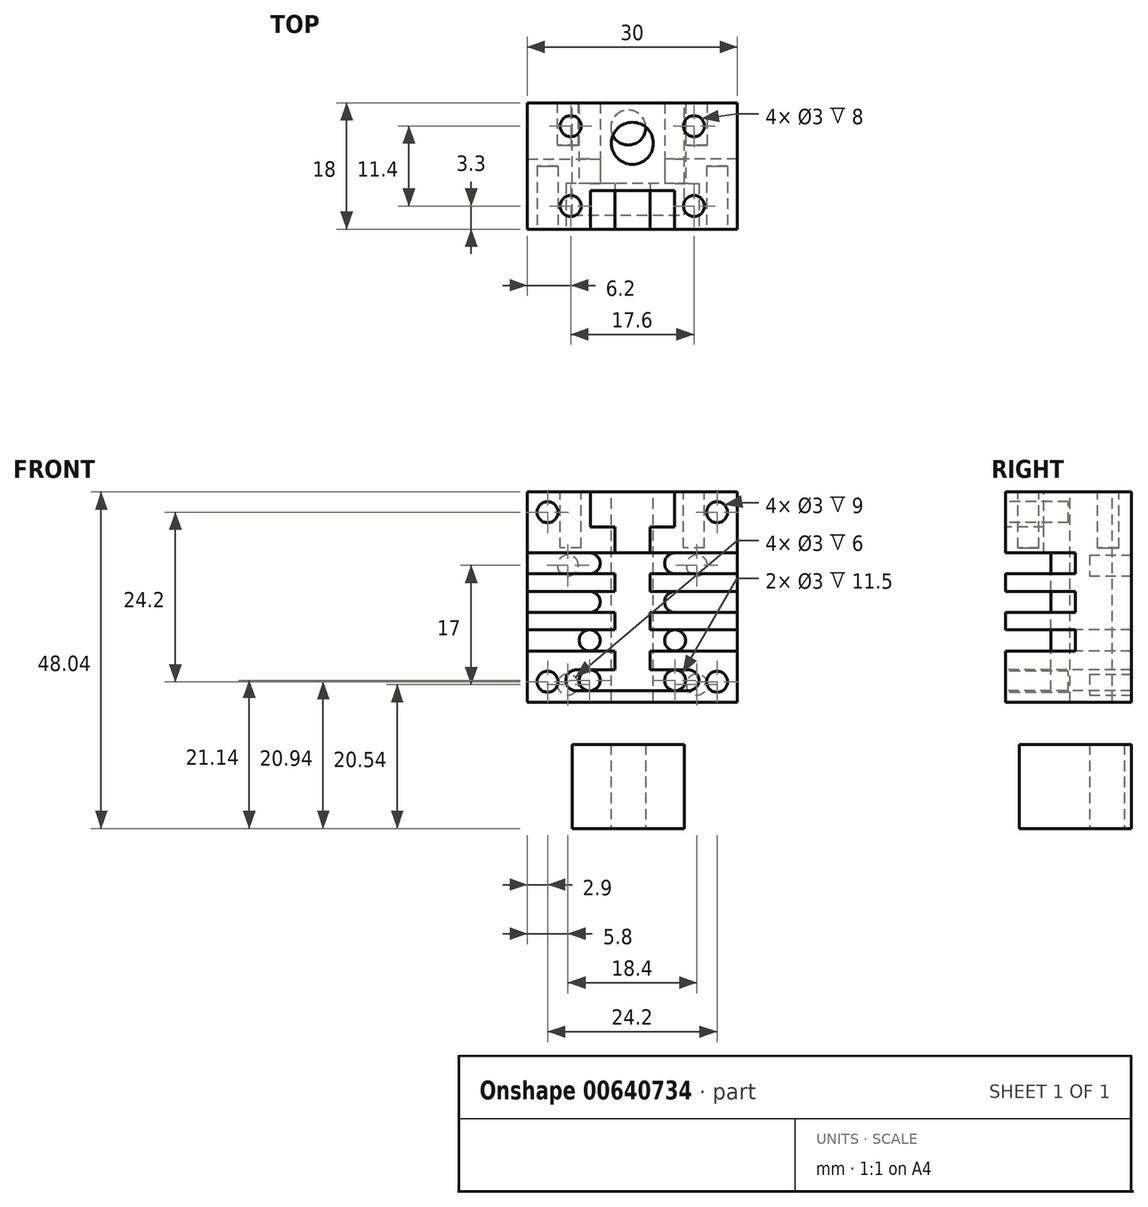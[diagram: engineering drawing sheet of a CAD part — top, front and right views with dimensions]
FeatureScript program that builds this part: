
annotation { "Feature Type Name" : "Feature", "Feature Type Description" : "" }
export const myFeature = defineFeature(function(context is Context, id is Id, definition is map)
    precondition{}
    {
        {
            var Q0;
            Q0=qCreatedBy(makeId("Front.planeOp"),FACE);
            var sketch = newSketch(context, id + "F0", { "sketchPlane" : qUnion([Q0])});
            skLineSegment(sketch, "E0.bottom", {"start": v(15, -15) * mm, "end": v(-15, -15) * mm});
            skLineSegment(sketch, "E0.top", {"start": v(15, 15) * mm, "end": v(-15, 15) * mm});
            skLineSegment(sketch, "E0.left", {"start": v(15, -15) * mm, "end": v(15, 15) * mm});
            skLineSegment(sketch, "E0.right", {"start": v(-15, -15) * mm, "end": v(-15, 15) * mm});
            skPoint(sketch, "E0.middle", {"position": v(0, 0) * mm});
            skSolve(sketch);
        }
        {
            var Q0;
            Q0 = qSketchRegion(id + "F0", true);
            extrude(context, id + "F1", {"entities" : qUnion([Q0]), "depth" : 18 * mm, "offsetDistance" : 25 * mm});
        }
        {
            var Q0;
            Q0=makeQuery(id+"F1.opExtrude","CAP_FACE",FACE,{"disambiguationData":[OSD([sQuery(id+"F0.wireOp",EDGE,"E0.bottom"),sQuery(id+"F0.wireOp",EDGE,"E0.top"),sQuery(id+"F0.wireOp",EDGE,"E0.left"),sQuery(id+"F0.wireOp",EDGE,"E0.right")])],"isStart":false});
            var sketch = newSketch(context, id + "F2", { "sketchPlane" : qUnion([Q0])});
            skLineSegment(sketch, "E1.bottom", {"start": v(6, 10) * mm, "end": v(-6, 10) * mm});
            skLineSegment(sketch, "E1.top", {"start": v(6, 20) * mm, "end": v(-6, 20) * mm});
            skLineSegment(sketch, "E1.left", {"start": v(6, 10) * mm, "end": v(6, 20) * mm});
            skLineSegment(sketch, "E1.right", {"start": v(-6, 10) * mm, "end": v(-6, 20) * mm});
            skPoint(sketch, "E1.middle", {"position": v(0, 15) * mm});
            skLineSegment(sketch, "E2.bottom", {"start": v(2.5, -13.4) * mm, "end": v(-2.5, -13.4) * mm});
            skLineSegment(sketch, "E2.top", {"start": v(2.5, 13.4) * mm, "end": v(-2.5, 13.4) * mm});
            skLineSegment(sketch, "E2.left", {"start": v(2.5, -13.4) * mm, "end": v(2.5, 13.4) * mm});
            skLineSegment(sketch, "E2.right", {"start": v(-2.5, -13.4) * mm, "end": v(-2.5, 13.4) * mm});
            skPoint(sketch, "E2.middle", {"position": v(0, 0) * mm});
            skSolve(sketch);
        }
        {
            var Q0;
            Q0 = qSketchRegion(id + "F2", true);
            extrude(context, id + "F3", {"entities" : qUnion([Q0]), "operationType" : NewBodyOperationType.REMOVE, "oppositeDirection" : true, "depth" : 5.5 * mm, "offsetDistance" : 25 * mm});
        }
        {
            var Q0;
            Q0=makeQuery(id+"F1.opExtrude","CAP_FACE",FACE,{"disambiguationData":[OSD([sQuery(id+"F0.wireOp",EDGE,"E0.bottom"),sQuery(id+"F0.wireOp",EDGE,"E0.top"),sQuery(id+"F0.wireOp",EDGE,"E0.left"),sQuery(id+"F0.wireOp",EDGE,"E0.right")])],"isStart":false});
            var sketch = newSketch(context, id + "F4", { "sketchPlane" : qUnion([Q0])});
            skLineSegment(sketch, "E3", {"start": v(13.15, -15) * mm, "end": v(13.15, -7.7) * mm, "construction": true});
            skLineSegment(sketch, "E4", {"start": v(13.15, -7.7) * mm, "end": v(13.15, -4.7) * mm, "construction": true});
            skLineSegment(sketch, "E5", {"start": v(13.15, -4.7) * mm, "end": v(13.15, -2.2) * mm, "construction": true});
            skLineSegment(sketch, "E6", {"start": v(13.15, -2.2) * mm, "end": v(13.15, 0.8) * mm, "construction": true});
            skLineSegment(sketch, "E7", {"start": v(13.15, 0.8) * mm, "end": v(13.15, 3.3) * mm, "construction": true});
            skLineSegment(sketch, "E8", {"start": v(13.15, 3.3) * mm, "end": v(13.15, 6.3) * mm, "construction": true});
            skLineSegment(sketch, "E9", {"start": v(13.15, 6.3) * mm, "end": v(13.15, 14.8) * mm, "construction": true});
            skLineSegment(sketch, "E10.bottom", {"start": v(15, -7.7) * mm, "end": v(-15, -7.7) * mm});
            skLineSegment(sketch, "E10.top", {"start": v(15, -4.7) * mm, "end": v(-15, -4.7) * mm});
            skLineSegment(sketch, "E10.left", {"start": v(15, -7.7) * mm, "end": v(15, -4.7) * mm});
            skLineSegment(sketch, "E10.right", {"start": v(-15, -7.7) * mm, "end": v(-15, -4.7) * mm});
            skLineSegment(sketch, "E11.bottom", {"start": v(15, -2.2) * mm, "end": v(-15, -2.2) * mm});
            skLineSegment(sketch, "E11.top", {"start": v(15, 0.8) * mm, "end": v(-15, 0.8) * mm});
            skLineSegment(sketch, "E11.left", {"start": v(15, -2.2) * mm, "end": v(15, 0.8) * mm});
            skLineSegment(sketch, "E11.right", {"start": v(-15, -2.2) * mm, "end": v(-15, 0.8) * mm});
            skLineSegment(sketch, "E12.bottom", {"start": v(15, 3.3) * mm, "end": v(-15, 3.3) * mm});
            skLineSegment(sketch, "E12.top", {"start": v(15, 6.3) * mm, "end": v(-15, 6.3) * mm});
            skLineSegment(sketch, "E12.left", {"start": v(15, 3.3) * mm, "end": v(15, 6.3) * mm});
            skLineSegment(sketch, "E12.right", {"start": v(-15, 3.3) * mm, "end": v(-15, 6.3) * mm});
            skPoint(sketch, "E13.startSnap0", {"position": v(13.15, -11.35) * mm});
            skLineSegment(sketch, "E14", {"start": v(0, -7.7) * mm, "end": v(0, -10.4) * mm, "construction": true});
            skLineSegment(sketch, "E15", {"start": v(0, -10.4) * mm, "end": v(0, -11.9) * mm, "construction": true});
            skLineSegment(sketch, "E16", {"start": v(8, -11.9) * mm, "end": v(15, -11.9) * mm, "construction": true});
            skLineSegment(sketch, "E17", {"start": v(8, -11.9) * mm, "end": v(-8, -11.9) * mm, "construction": true});
            skArc(sketch, "E18.0.startCap", {"start": v(8, -10.4) * mm, "mid": v(9.5, -11.9) * mm, "end": v(8, -13.4) * mm});
            skArc(sketch, "E18.0.endCap", {"start": v(-8, -13.4) * mm, "mid": v(-9.5, -11.9) * mm, "end": v(-8, -10.4) * mm});
            skLineSegment(sketch, "E18.0.left", {"start": v(8, -13.4) * mm, "end": v(-8, -13.4) * mm});
            skLineSegment(sketch, "E18.0.right", {"start": v(8, -10.4) * mm, "end": v(-8, -10.4) * mm});
            skLineSegment(sketch, "E19", {"start": v(2.5, 3.3) * mm, "end": v(2.5, 0.8) * mm});
            skLineSegment(sketch, "E20", {"start": v(2.5, -2.2) * mm, "end": v(2.5, -4.7) * mm});
            skLineSegment(sketch, "E21", {"start": v(-2.5, 3.3) * mm, "end": v(-2.5, 0.8) * mm});
            skLineSegment(sketch, "E22", {"start": v(-2.5, -2.2) * mm, "end": v(-2.5, -4.7) * mm});
            skLineSegment(sketch, "E23", {"start": v(2.5, -7.7) * mm, "end": v(2.5, -10.4) * mm});
            skLineSegment(sketch, "E24", {"start": v(-2.5, -7.7) * mm, "end": v(-2.5, -10.4) * mm});
            skSolve(sketch);
        }
        {
            var Q0;
            Q0 = qSketchRegion(id + "F4", true);
            extrude(context, id + "F5", {"entities" : qUnion([Q0]), "operationType" : NewBodyOperationType.REMOVE, "oppositeDirection" : true, "depth" : 6.5 * mm, "offsetDistance" : 25 * mm});
        }
        {
            var Q0;
            Q0=makeQuery(id+"F5.boolean.opBoolean","COPY",FACE,{"derivedFrom":makeQuery(id+"F5.opExtrude","CAP_FACE",FACE,{"disambiguationData":[OSD([sQuery(id+"F4.wireOp",EDGE,"E10.bottom"),sQuery(id+"F4.wireOp",EDGE,"E10.top"),sQuery(id+"F4.wireOp",EDGE,"E10.left"),sQuery(id+"F4.wireOp",EDGE,"E10.right"),sQuery(id+"F4.wireOp",EDGE,"E11.bottom"),sQuery(id+"F4.wireOp",EDGE,"E11.top"),sQuery(id+"F4.wireOp",EDGE,"E11.left"),sQuery(id+"F4.wireOp",EDGE,"E11.right"),sQuery(id+"F4.wireOp",EDGE,"E12.bottom"),sQuery(id+"F4.wireOp",EDGE,"E12.top"),sQuery(id+"F4.wireOp",EDGE,"E12.left"),sQuery(id+"F4.wireOp",EDGE,"E12.right"),sQuery(id+"F4.wireOp",EDGE,"E18.0.startCap"),sQuery(id+"F4.wireOp",EDGE,"E18.0.endCap"),sQuery(id+"F4.wireOp",EDGE,"E18.0.left"),sQuery(id+"F4.wireOp",EDGE,"E18.0.right"),sQuery(id+"F4.wireOp",EDGE,"E19"),sQuery(id+"F4.wireOp",EDGE,"E20"),sQuery(id+"F4.wireOp",EDGE,"E21"),sQuery(id+"F4.wireOp",EDGE,"E22"),sQuery(id+"F4.wireOp",EDGE,"E23"),sQuery(id+"F4.wireOp",EDGE,"E24")])],"isStart":false})});
            var sketch = newSketch(context, id + "F6", { "sketchPlane" : qUnion([Q0])});
            skLineSegment(sketch, "E25", {"start": v(-17, 4.8) * mm, "end": v(-6.1, 4.8) * mm, "construction": true});
            skPoint(sketch, "E25.startSnap0", {"position": v(-15, 4.8) * mm});
            skLineSegment(sketch, "E26", {"start": v(-17, -0.7) * mm, "end": v(-6.1, -0.7) * mm, "construction": true});
            skPoint(sketch, "E26.startSnap0", {"position": v(-15, -0.7) * mm});
            skLineSegment(sketch, "E27", {"start": v(-17, -6.2) * mm, "end": v(-6.1, -6.2) * mm, "construction": true});
            skPoint(sketch, "E27.startSnap0", {"position": v(-15, -6.2) * mm});
            skLineSegment(sketch, "E28", {"start": v(17, 4.8) * mm, "end": v(6.1, 4.8) * mm, "construction": true});
            skPoint(sketch, "E28.startSnap0", {"position": v(15, 4.8) * mm});
            skLineSegment(sketch, "E29", {"start": v(17, -0.7) * mm, "end": v(6.1, -0.7) * mm, "construction": true});
            skPoint(sketch, "E29.startSnap0", {"position": v(15, -0.7) * mm});
            skLineSegment(sketch, "E30", {"start": v(17, -6.2) * mm, "end": v(6.1, -6.2) * mm, "construction": true});
            skPoint(sketch, "E30.startSnap0", {"position": v(15, -6.2) * mm});
            skArc(sketch, "E31.0.startCap", {"start": v(-17, 3.3) * mm, "mid": v(-18.5, 4.8) * mm, "end": v(-17, 6.3) * mm});
            skArc(sketch, "E31.0.endCap", {"start": v(-6.1, 6.3) * mm, "mid": v(-4.6, 4.8) * mm, "end": v(-6.1, 3.3) * mm});
            skLineSegment(sketch, "E31.0.left", {"start": v(-17, 6.3) * mm, "end": v(-6.1, 6.3) * mm});
            skLineSegment(sketch, "E31.0.right", {"start": v(-17, 3.3) * mm, "end": v(-6.1, 3.3) * mm});
            skArc(sketch, "E31.1.startCap", {"start": v(-17, -2.2) * mm, "mid": v(-18.5, -0.7) * mm, "end": v(-17, 0.8) * mm});
            skArc(sketch, "E31.1.endCap", {"start": v(-6.1, 0.8) * mm, "mid": v(-4.6, -0.7) * mm, "end": v(-6.1, -2.2) * mm});
            skLineSegment(sketch, "E31.1.left", {"start": v(-17, 0.8) * mm, "end": v(-6.1, 0.8) * mm});
            skLineSegment(sketch, "E31.1.right", {"start": v(-17, -2.2) * mm, "end": v(-6.1, -2.2) * mm});
            skArc(sketch, "E31.2.startCap", {"start": v(-17, -7.7) * mm, "mid": v(-18.5, -6.2) * mm, "end": v(-17, -4.7) * mm});
            skArc(sketch, "E31.2.endCap", {"start": v(-6.1, -4.7) * mm, "mid": v(-4.6, -6.2) * mm, "end": v(-6.1, -7.7) * mm});
            skLineSegment(sketch, "E31.2.left", {"start": v(-17, -4.7) * mm, "end": v(-6.1, -4.7) * mm});
            skLineSegment(sketch, "E31.2.right", {"start": v(-17, -7.7) * mm, "end": v(-6.1, -7.7) * mm});
            skArc(sketch, "E31.3.startCap", {"start": v(17, 6.3) * mm, "mid": v(18.5, 4.8) * mm, "end": v(17, 3.3) * mm});
            skArc(sketch, "E31.3.endCap", {"start": v(6.1, 3.3) * mm, "mid": v(4.6, 4.8) * mm, "end": v(6.1, 6.3) * mm});
            skLineSegment(sketch, "E31.3.left", {"start": v(17, 3.3) * mm, "end": v(6.1, 3.3) * mm});
            skLineSegment(sketch, "E31.3.right", {"start": v(17, 6.3) * mm, "end": v(6.1, 6.3) * mm});
            skArc(sketch, "E31.4.startCap", {"start": v(17, 0.8) * mm, "mid": v(18.5, -0.7) * mm, "end": v(17, -2.2) * mm});
            skArc(sketch, "E31.4.endCap", {"start": v(6.1, -2.2) * mm, "mid": v(4.6, -0.7) * mm, "end": v(6.1, 0.8) * mm});
            skLineSegment(sketch, "E31.4.left", {"start": v(17, -2.2) * mm, "end": v(6.1, -2.2) * mm});
            skLineSegment(sketch, "E31.4.right", {"start": v(17, 0.8) * mm, "end": v(6.1, 0.8) * mm});
            skArc(sketch, "E31.5.startCap", {"start": v(17, -4.7) * mm, "mid": v(18.5, -6.2) * mm, "end": v(17, -7.7) * mm});
            skArc(sketch, "E31.5.endCap", {"start": v(6.1, -7.7) * mm, "mid": v(4.6, -6.2) * mm, "end": v(6.1, -4.7) * mm});
            skLineSegment(sketch, "E31.5.left", {"start": v(17, -7.7) * mm, "end": v(6.1, -7.7) * mm});
            skLineSegment(sketch, "E31.5.right", {"start": v(17, -4.7) * mm, "end": v(6.1, -4.7) * mm});
            skSolve(sketch);
        }
        {
            var Q0;
            Q0 = qSketchRegion(id + "F6", true);
            extrude(context, id + "F7", {"entities" : qUnion([Q0]), "operationType" : NewBodyOperationType.REMOVE, "oppositeDirection" : true, "depth" : 3.5 * mm, "offsetDistance" : 25 * mm});
        }
        {
            var Q0;
            {var subQ0=sQuery(id+"F2.wireOp",EDGE,"E1.right");var subQ3=sQuery(id+"F0.wireOp",EDGE,"E0.right");var subQ4=sQuery(id+"F0.wireOp",EDGE,"E0.top");Q0=makeQuery(id+"F5.boolean.opBoolean","SPLIT",FACE,{"disambiguationData":[TD([makeQuery(id+"F3.boolean.opBoolean","COPY",FACE,{"derivedFrom":makeQuery(id+"F3.opExtrude","SWEPT_FACE",FACE,{"disambiguationData":[OSD([subQ0])]})})])],"derivedFrom":makeQuery(id+"F1.opExtrude","CAP_FACE",FACE,{"disambiguationData":[OSD([sQuery(id+"F0.wireOp",EDGE,"E0.bottom"),subQ4,sQuery(id+"F0.wireOp",EDGE,"E0.left"),subQ3])],"isStart":false})});}
            var sketch = newSketch(context, id + "F8", { "sketchPlane" : qUnion([Q0])});
            skLineSegment(sketch, "E32", {"start": v(-12.1, 12.1) * mm, "end": v(12.1, 12.1) * mm, "construction": true});
            skLineSegment(sketch, "E33", {"start": v(12.1, 12.1) * mm, "end": v(12.1, -12.1) * mm, "construction": true});
            skLineSegment(sketch, "E34", {"start": v(-12.1, 12.1) * mm, "end": v(-15, 12.1) * mm, "construction": true});
            skLineSegment(sketch, "E35", {"start": v(12.1, 12.1) * mm, "end": v(15, 12.1) * mm, "construction": true});
            skLineSegment(sketch, "E36", {"start": v(12.1, 12.1) * mm, "end": v(12.1, 15) * mm, "construction": true});
            skLineSegment(sketch, "E37", {"start": v(12.1, -12.1) * mm, "end": v(12.1, -15) * mm, "construction": true});
            skCircle(sketch, "E38", {"center": v(-12.1, 12.1) * mm, "radius": 1.5 * mm});
            skCircle(sketch, "E39", {"center": v(12.1, 12.1) * mm, "radius": 1.5 * mm});
            skCircle(sketch, "E40", {"center": v(12.1, -12.1) * mm, "radius": 1.5 * mm});
            skCircle(sketch, "E41", {"center": v(-12.1, -12.1) * mm, "radius": 1.5 * mm});
            skSolve(sketch);
        }
        {
            var Q0;
            Q0 = qSketchRegion(id + "F8", true);
            extrude(context, id + "F9", {"entities" : qUnion([Q0]), "operationType" : NewBodyOperationType.REMOVE, "oppositeDirection" : true, "depth" : 9 * mm, "offsetDistance" : 25 * mm});
        }
        {
            var Q0;
            Q0=makeQuery(id+"F5.boolean.opBoolean","COPY",FACE,{"derivedFrom":makeQuery(id+"F5.opExtrude","CAP_FACE",FACE,{"disambiguationData":[OSD([sQuery(id+"F4.wireOp",EDGE,"E10.bottom"),sQuery(id+"F4.wireOp",EDGE,"E10.top"),sQuery(id+"F4.wireOp",EDGE,"E10.left"),sQuery(id+"F4.wireOp",EDGE,"E10.right"),sQuery(id+"F4.wireOp",EDGE,"E11.bottom"),sQuery(id+"F4.wireOp",EDGE,"E11.top"),sQuery(id+"F4.wireOp",EDGE,"E11.left"),sQuery(id+"F4.wireOp",EDGE,"E11.right"),sQuery(id+"F4.wireOp",EDGE,"E12.bottom"),sQuery(id+"F4.wireOp",EDGE,"E12.top"),sQuery(id+"F4.wireOp",EDGE,"E12.left"),sQuery(id+"F4.wireOp",EDGE,"E12.right"),sQuery(id+"F4.wireOp",EDGE,"E18.0.startCap"),sQuery(id+"F4.wireOp",EDGE,"E18.0.endCap"),sQuery(id+"F4.wireOp",EDGE,"E18.0.left"),sQuery(id+"F4.wireOp",EDGE,"E18.0.right"),sQuery(id+"F4.wireOp",EDGE,"E19"),sQuery(id+"F4.wireOp",EDGE,"E20"),sQuery(id+"F4.wireOp",EDGE,"E21"),sQuery(id+"F4.wireOp",EDGE,"E22"),sQuery(id+"F4.wireOp",EDGE,"E23"),sQuery(id+"F4.wireOp",EDGE,"E24")])],"isStart":false})});
            var sketch = newSketch(context, id + "F10", { "sketchPlane" : qUnion([Q0])});
            skCircle(sketch, "E42", {"center": v(6.1, -6.2) * mm, "radius": 1.5 * mm});
            skCircle(sketch, "E43", {"center": v(-6.1, -6.2) * mm, "radius": 1.5 * mm});
            skCircle(sketch, "E44", {"center": v(-6.1, -11.9) * mm, "radius": 1.5 * mm});
            skPoint(sketch, "E44.centerSnap0", {"position": v(-9.5, -11.9) * mm});
            skCircle(sketch, "E45", {"center": v(6.1, -11.9) * mm, "radius": 1.5 * mm});
            skSolve(sketch);
        }
        {
            var Q0;
            Q0 = qSketchRegion(id + "F10", true);
            extrude(context, id + "F11", {"entities" : qUnion([Q0]), "operationType" : NewBodyOperationType.REMOVE, "oppositeDirection" : true, "depth" : 25 * mm, "offsetDistance" : 25 * mm});
        }
        {
            var Q0;
            Q0=makeQuery(id+"F1.opExtrude","CAP_FACE",FACE,{"disambiguationData":[OSD([sQuery(id+"F0.wireOp",EDGE,"E0.bottom"),sQuery(id+"F0.wireOp",EDGE,"E0.top"),sQuery(id+"F0.wireOp",EDGE,"E0.left"),sQuery(id+"F0.wireOp",EDGE,"E0.right")])],"isStart":true});
            var sketch = newSketch(context, id + "F12", { "sketchPlane" : qUnion([Q0])});
            skLineSegment(sketch, "E46", {"start": v(9.2, -15) * mm, "end": v(9.2, -12.5) * mm, "construction": true});
            skLineSegment(sketch, "E47", {"start": v(9.2, -12.5) * mm, "end": v(15, -12.5) * mm, "construction": true});
            skLineSegment(sketch, "E48", {"start": v(-15, -12.5) * mm, "end": v(-9.2, -12.5) * mm, "construction": true});
            skLineSegment(sketch, "E49", {"start": v(9.2, -12.5) * mm, "end": v(9.2, 4.5) * mm, "construction": true});
            skCircle(sketch, "E50", {"center": v(9.2, -12.5) * mm, "radius": 1.5 * mm});
            skCircle(sketch, "E51", {"center": v(9.2, 4.5) * mm, "radius": 1.5 * mm});
            skCircle(sketch, "E52", {"center": v(-9.2, -12.5) * mm, "radius": 1.5 * mm});
            skCircle(sketch, "E53", {"center": v(-9.2, 4.5) * mm, "radius": 1.5 * mm});
            skSolve(sketch);
        }
        {
            var Q0;
            Q0 = qSketchRegion(id + "F12", true);
            extrude(context, id + "F13", {"entities" : qUnion([Q0]), "operationType" : NewBodyOperationType.REMOVE, "oppositeDirection" : true, "depth" : 6 * mm, "offsetDistance" : 25 * mm});
        }
        {
            var Q0;
            Q0=makeQuery(id+"F1.opExtrude","SWEPT_FACE",FACE,{"disambiguationData":[OSD([sQuery(id+"F0.wireOp",EDGE,"E0.top")])]});
            var sketch = newSketch(context, id + "F14", { "sketchPlane" : qUnion([Q0])});
            skLineSegment(sketch, "E54", {"start": v(-15, -3.3) * mm, "end": v(-8.8, -3.3) * mm, "construction": true});
            skLineSegment(sketch, "E55", {"start": v(-8.8, -3.3) * mm, "end": v(-8.8, 0) * mm, "construction": true});
            skLineSegment(sketch, "E56", {"start": v(-8.8, -3.3) * mm, "end": v(8.8, -3.3) * mm, "construction": true});
            skLineSegment(sketch, "E57", {"start": v(-8.8, -3.3) * mm, "end": v(-8.8, -14.7) * mm, "construction": true});
            skLineSegment(sketch, "E58", {"start": v(8.8, -3.3) * mm, "end": v(15, -3.3) * mm, "construction": true});
            skLineSegment(sketch, "E59", {"start": v(-8.8, -14.7) * mm, "end": v(-8.8, -18) * mm, "construction": true});
            skCircle(sketch, "E60", {"center": v(-8.8, -3.3) * mm, "radius": 1.5 * mm});
            skCircle(sketch, "E61", {"center": v(8.8, -3.3) * mm, "radius": 1.5 * mm});
            skCircle(sketch, "E62", {"center": v(-8.8, -14.7) * mm, "radius": 1.5 * mm});
            skCircle(sketch, "E63", {"center": v(8.8, -14.7) * mm, "radius": 1.5 * mm});
            skSolve(sketch);
        }
        {
            var Q0;
            Q0 = qSketchRegion(id + "F14", true);
            extrude(context, id + "F15", {"entities" : qUnion([Q0]), "operationType" : NewBodyOperationType.REMOVE, "oppositeDirection" : true, "depth" : 8 * mm, "offsetDistance" : 25 * mm});
        }
        {
            var Q0;
            Q0=qCreatedBy(makeId("Front.planeOp"),FACE);
            var sketch = newSketch(context, id + "F16", { "sketchPlane" : qUnion([Q0])});
            skLineSegment(sketch, "E64.bottom", {"start": v(-8.58, -21.04) * mm, "end": v(7.42, -21.04) * mm});
            skLineSegment(sketch, "E64.top", {"start": v(-8.58, -33.04) * mm, "end": v(7.42, -33.04) * mm});
            skLineSegment(sketch, "E64.left", {"start": v(-8.58, -21.04) * mm, "end": v(-8.58, -33.04) * mm});
            skLineSegment(sketch, "E64.right", {"start": v(7.42, -21.04) * mm, "end": v(7.42, -33.04) * mm});
            skSolve(sketch);
        }
        {
            var Q0;
            Q0 = qSketchRegion(id + "F16", true);
            extrude(context, id + "F17", {"entities" : qUnion([Q0]), "depth" : 16 * mm, "offsetDistance" : 25 * mm});
        }
        {
            var Q0;
            Q0=makeQuery(id+"F1.opExtrude","SWEPT_FACE",FACE,{"disambiguationData":[OSD([sQuery(id+"F0.wireOp",EDGE,"E0.top")])]});
            var sketch = newSketch(context, id + "F18", { "sketchPlane" : qUnion([Q0])});
            skLineSegment(sketch, "E65", {"start": v(0, 0) * mm, "end": v(0, -5.75) * mm, "construction": true});
            skPoint(sketch, "E65.endSnap0", {"position": v(0, 0) * mm});
            skCircle(sketch, "E66", {"center": v(0, -5.75) * mm, "radius": 3 * mm});
            skSolve(sketch);
        }
        {
            var Q0;
            Q0 = qSketchRegion(id + "F18", true);
            extrude(context, id + "F19", {"entities" : qUnion([Q0]), "operationType" : NewBodyOperationType.REMOVE, "oppositeDirection" : true, "depth" : 30 * mm, "offsetDistance" : 25 * mm});
        }
        {
            var Q0;
            Q0=makeQuery(id+"F17.opExtrude","SWEPT_FACE",FACE,{"disambiguationData":[OSD([sQuery(id+"F16.wireOp",EDGE,"E64.top")])]});
            var sketch = newSketch(context, id + "F20", { "sketchPlane" : qUnion([Q0])});
            skLineSegment(sketch, "E67", {"start": v(-0.58, 0) * mm, "end": v(-0.58, 3.5) * mm, "construction": true});
            skCircle(sketch, "E68", {"center": v(-0.58, 3.5) * mm, "radius": 2.5 * mm});
            skSolve(sketch);
        }
        {
            var Q0;
            Q0 = qSketchRegion(id + "F20", true);
            extrude(context, id + "F21", {"entities" : qUnion([Q0]), "operationType" : NewBodyOperationType.REMOVE, "oppositeDirection" : true, "depth" : 12 * mm, "offsetDistance" : 25 * mm});
        }
    });
